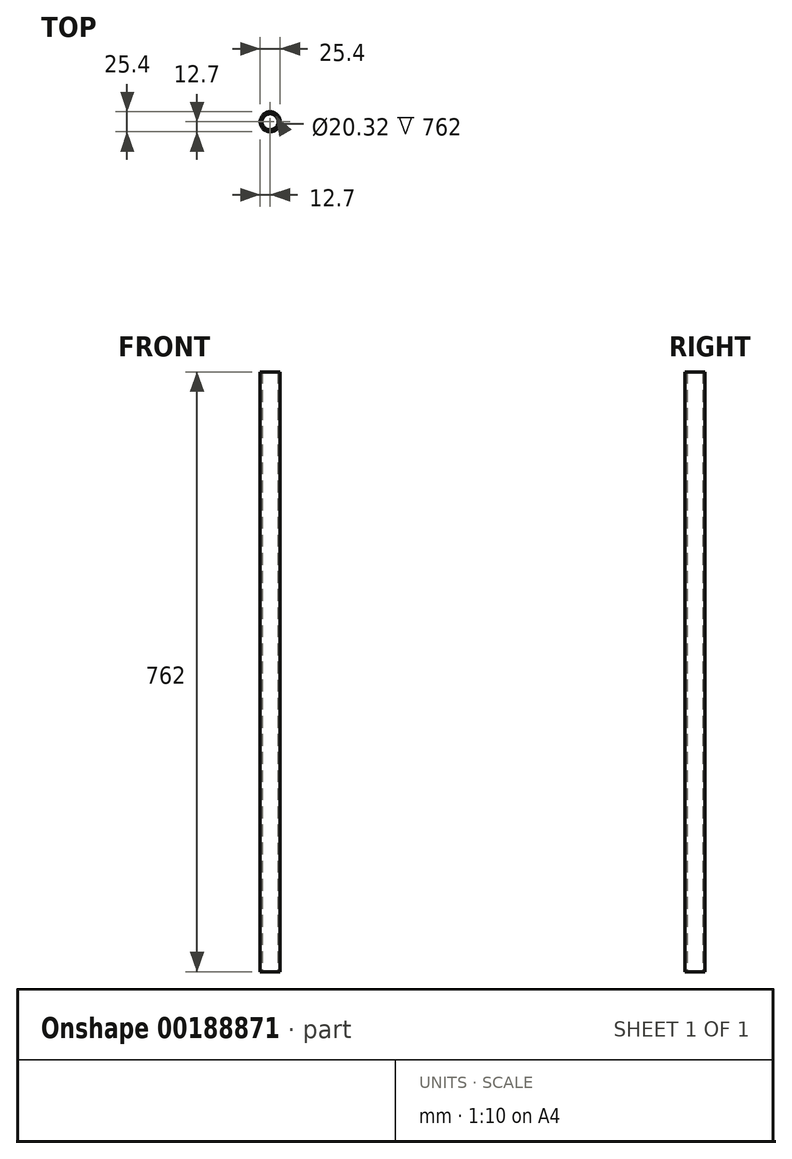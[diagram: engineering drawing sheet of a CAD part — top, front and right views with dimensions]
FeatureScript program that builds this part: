
annotation { "Feature Type Name" : "Feature", "Feature Type Description" : "" }
export const myFeature = defineFeature(function(context is Context, id is Id, definition is map)
    precondition{}
    {
        {
            var Q0;
            Q0=qCreatedBy(makeId("Top.planeOp"),FACE);
            var sketch = newSketch(context, id + "F0", { "sketchPlane" : qUnion([Q0])});
            skCircle(sketch, "E0", {"center": v(0, 0) * mm, "radius": 12.7 * mm});
            skCircle(sketch, "E1", {"center": v(0, 0) * mm, "radius": 10.16 * mm});
            skSolve(sketch);
        }
        {
            var Q0;
            Q0 = qSketchRegion(id + "F0", true);
            extrude(context, id + "F1", {"entities" : qUnion([Q0]), "depth" : 762 * mm});
        }
    });
